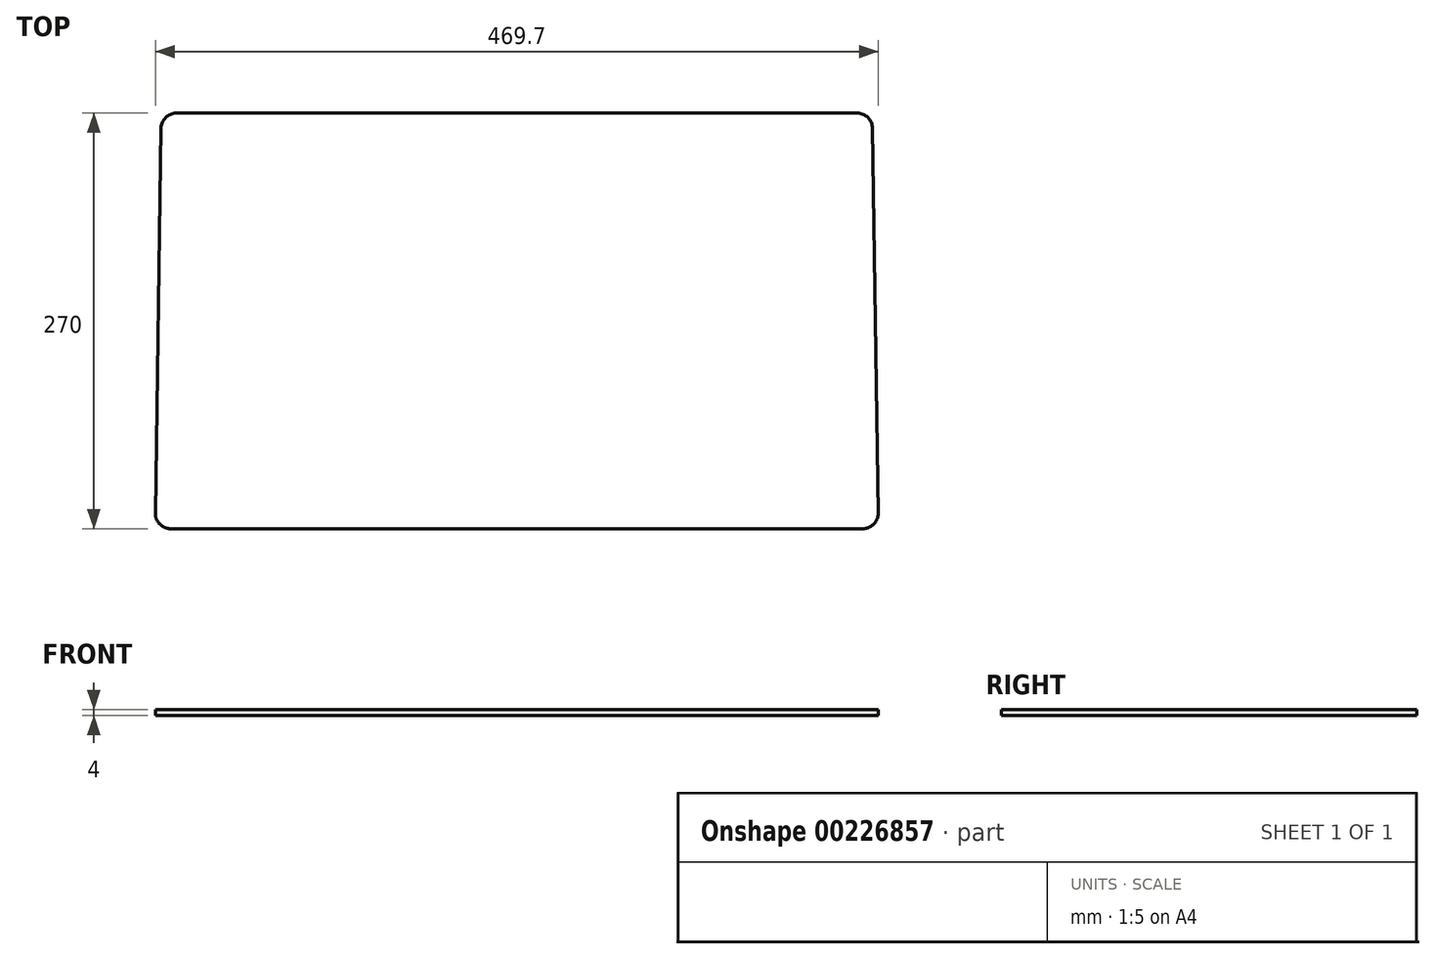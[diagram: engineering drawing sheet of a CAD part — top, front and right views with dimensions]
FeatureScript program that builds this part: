
annotation { "Feature Type Name" : "Feature", "Feature Type Description" : "" }
export const myFeature = defineFeature(function(context is Context, id is Id, definition is map)
    precondition{}
    {
        {
            var Q0;
            Q0=qCreatedBy(makeId("Top.planeOp"),FACE);
            var sketch = newSketch(context, id + "F0", { "sketchPlane" : qUnion([Q0])});
            skLineSegment(sketch, "E0", {"start": v(-224.85, 0) * mm, "end": v(224.85, 0) * mm});
            skLineSegment(sketch, "E1", {"start": v(234.85, 10.15) * mm, "end": v(231.15, 260.15) * mm});
            skLineSegment(sketch, "E2", {"start": v(221.15, 270) * mm, "end": v(-221.15, 270) * mm});
            skLineSegment(sketch, "E3", {"start": v(-231.15, 260.15) * mm, "end": v(-234.85, 10.15) * mm});
            skPoint(sketch, "E4", {"position": v(0, 0) * mm});
            skLineSegment(sketch, "E5", {"start": v(0, 0) * mm, "end": v(0, 270) * mm, "construction": true});
            skPoint(sketch, "E6.visualSharp", {"position": v(-231, 270) * mm});
            skArc(sketch, "E6.filletArc", {"start": v(-221.15, 270) * mm, "mid": v(-228.17, 267.12) * mm, "end": v(-231.15, 260.15) * mm});
            skPoint(sketch, "E7.visualSharp", {"position": v(231, 270) * mm});
            skArc(sketch, "E7.filletArc", {"start": v(231.15, 260.15) * mm, "mid": v(228.17, 267.12) * mm, "end": v(221.15, 270) * mm});
            skPoint(sketch, "E8.visualSharp", {"position": v(235, 0) * mm});
            skArc(sketch, "E8.filletArc", {"start": v(224.85, 0) * mm, "mid": v(231.97, 2.98) * mm, "end": v(234.85, 10.15) * mm});
            skPoint(sketch, "E9.visualSharp", {"position": v(-235, 0) * mm});
            skArc(sketch, "E9.filletArc", {"start": v(-234.85, 10.15) * mm, "mid": v(-231.97, 2.98) * mm, "end": v(-224.85, 0) * mm});
            skSolve(sketch);
        }
        {
            var Q0;
            Q0=makeQuery(id+"F0.imprint","IMPRINT",FACE,{"disambiguationData":[TD([[makeQuery(id+"F0.imprint","IMPRINT",EDGE,{"derivedFrom":sQuery(id+"F0.wireOp",EDGE,"E0")}),1.0]])]});
            extrude(context, id + "F1", {"entities" : qUnion([Q0]), "depth" : 4 * mm});
        }
    });
